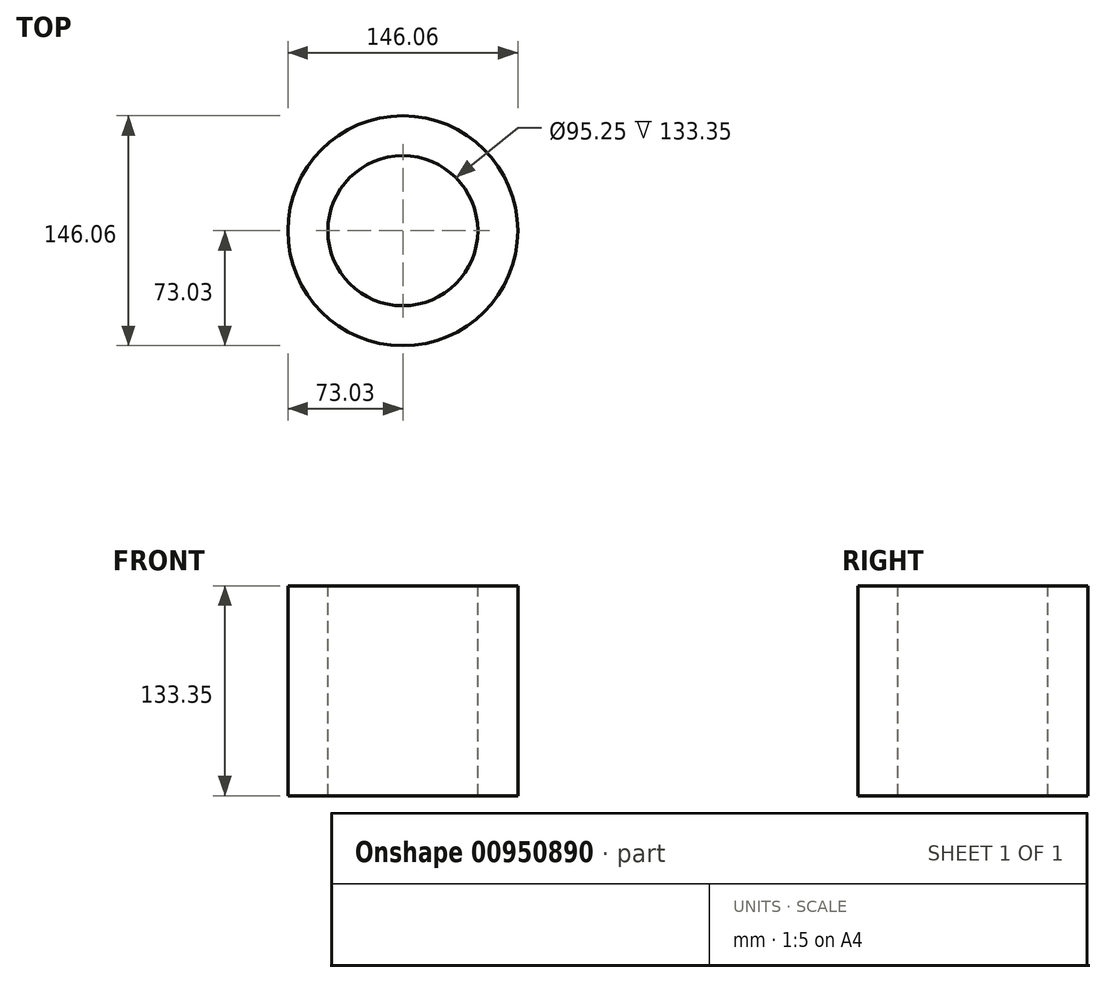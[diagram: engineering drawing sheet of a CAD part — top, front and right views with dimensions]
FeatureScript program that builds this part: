
annotation { "Feature Type Name" : "Feature", "Feature Type Description" : "" }
export const myFeature = defineFeature(function(context is Context, id is Id, definition is map)
    precondition{}
    {
        {
            var Q0;
            Q0=qCreatedBy(makeId("Front.planeOp"),FACE);
            var sketch = newSketch(context, id + "F0", { "sketchPlane" : qUnion([Q0])});
            skLineSegment(sketch, "E0", {"start": v(-73.03, 55.05) * mm, "end": v(-73.02, -78.3) * mm});
            skLineSegment(sketch, "E1", {"start": v(-73.02, -78.3) * mm, "end": v(-47.62, -78.3) * mm});
            skLineSegment(sketch, "E2", {"start": v(-47.62, -78.3) * mm, "end": v(-47.63, 55.05) * mm});
            skLineSegment(sketch, "E3", {"start": v(-73.03, 55.05) * mm, "end": v(-47.63, 55.05) * mm});
            skLineSegment(sketch, "E4", {"start": v(0, 104.4) * mm, "end": v(0, -121.13) * mm, "construction": true});
            skSolve(sketch);
        }
        {
            var Q0;
            Q0=makeQuery(id+"F0.imprint","IMPRINT",FACE,{"disambiguationData":[TD([[makeQuery(id+"F0.imprint","IMPRINT",EDGE,{"derivedFrom":sQuery(id+"F0.wireOp",EDGE,"E0")}),1.0]])]});
            var Q1;
            Q1=sQuery(id+"F0.wireOp",EDGE,"E4");
            revolve(context, id + "F1", {"surfaceOperationType" : NewSurfaceOperationType.NEW, "entities" : qUnion([Q0]), "axis" : qUnion([Q1]), "revolveType" : RevolveType.FULL});
        }
    });
